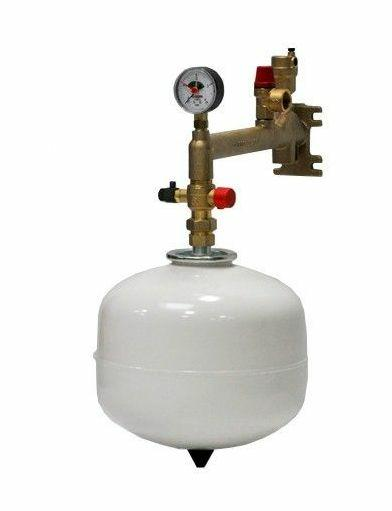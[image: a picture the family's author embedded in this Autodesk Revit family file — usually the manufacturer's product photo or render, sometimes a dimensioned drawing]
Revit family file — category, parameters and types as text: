
# Revit family: NLRS_50_FB_PIA_veiligheidspakket SPP_alpha innotec_nathan
name_source: partatom
category: Pipe Accessories
revit_build: Autodesk Revit 2017 (Build: 20160225_1515(x64)
units: mm (PartAtom-declared; Revit-internal decimal feet)

## family parameters
Cut with Voids When Loaded = No
Host = Face
OmniClass Number = 23.75.70.11.14
OmniClass Title = Expansion Vessels
Part Type = Normal
Round Connector Dimension = Use Diameter
Shared = Yes

## types (3) — shared parameters
Clearance Zone Top = 980 mm
Default Elevation = 1219 mm
IfcExportAs = ifcexpansion
IfcExportType = EXPANSION
Manufacturer = Alpha innotec
NLRS_C_breedte = 280 mm
NLRS_C_code_ETIM = EC012266
NLRS_C_code_fabrikant_gln = 2220000057042
NLRS_C_content_datum_uitgifte = 24-07-2019
NLRS_C_content_provider = Nathan Systems
NLRS_C_content_versie = 1.0
NLRS_C_diameter = 280 mm
NLRS_C_dikte = 440 mm
NLRS_C_materiaal = NLRS_h6_messing
Type Image = <None>
URL = https://www.nathan.nl

## per-type parameters (varying)
| type | Description | Model | NLRS_C_code_product | NLRS_C_description | NLRS_C_hoogte | NTN_C_type_index | SPP12 | SPP18 | SPP24 | Type Comments |
| Alpha innotec SPP12 | Alpha innotec veiligheidspakket primair 12 | SPP 12 | 150892VS01 | Alpha innotec veiligheidspakket primair 12 | 540 mm | 1 | Yes | No | No | Veiligheidspakket primair 12: Expansievat 12 liter met wandhouder (galg), kapafsluiter, veiligheidsgroep (veiligheids ventiel, manometer, autom. ontluchter) Vermogens 4–10 kW |
| Alpha innotec SPP18 | Alpha innotec veiligheidspakket primair 18 | SPP 18 | 150893VS01 | Alpha innotec veiligheidspakket primair 18 | 660 mm | 2 | No | Yes | No | Veiligheidspakket primair 18: Expansievat 18 liter met wandhouder (galg), kapafsluiter, veiligheidsgroep (veiligheids ventiel, manometer, autom. ontluchter) Vermogens 12–19 kW |
| Alpha innotec SPP24 | Alpha innotec veiligheidspakket primair 24 | SPP 24 | 150894VS01 | Alpha innotec veiligheidspakket primair 24 | 760 mm | 3 | No | No | Yes | Veiligheidspakket primair 24: Expansievat 24 liter met wandhouder (galg), kapafsluiter, veiligheidsgroep (veiligheids ventiel, manometer, autom. ontluchter) Vermogens 23-30 kW |

## geometry (parser evidence)
native form markers: Sweep x2
no freeform markers — native parametric forms only
